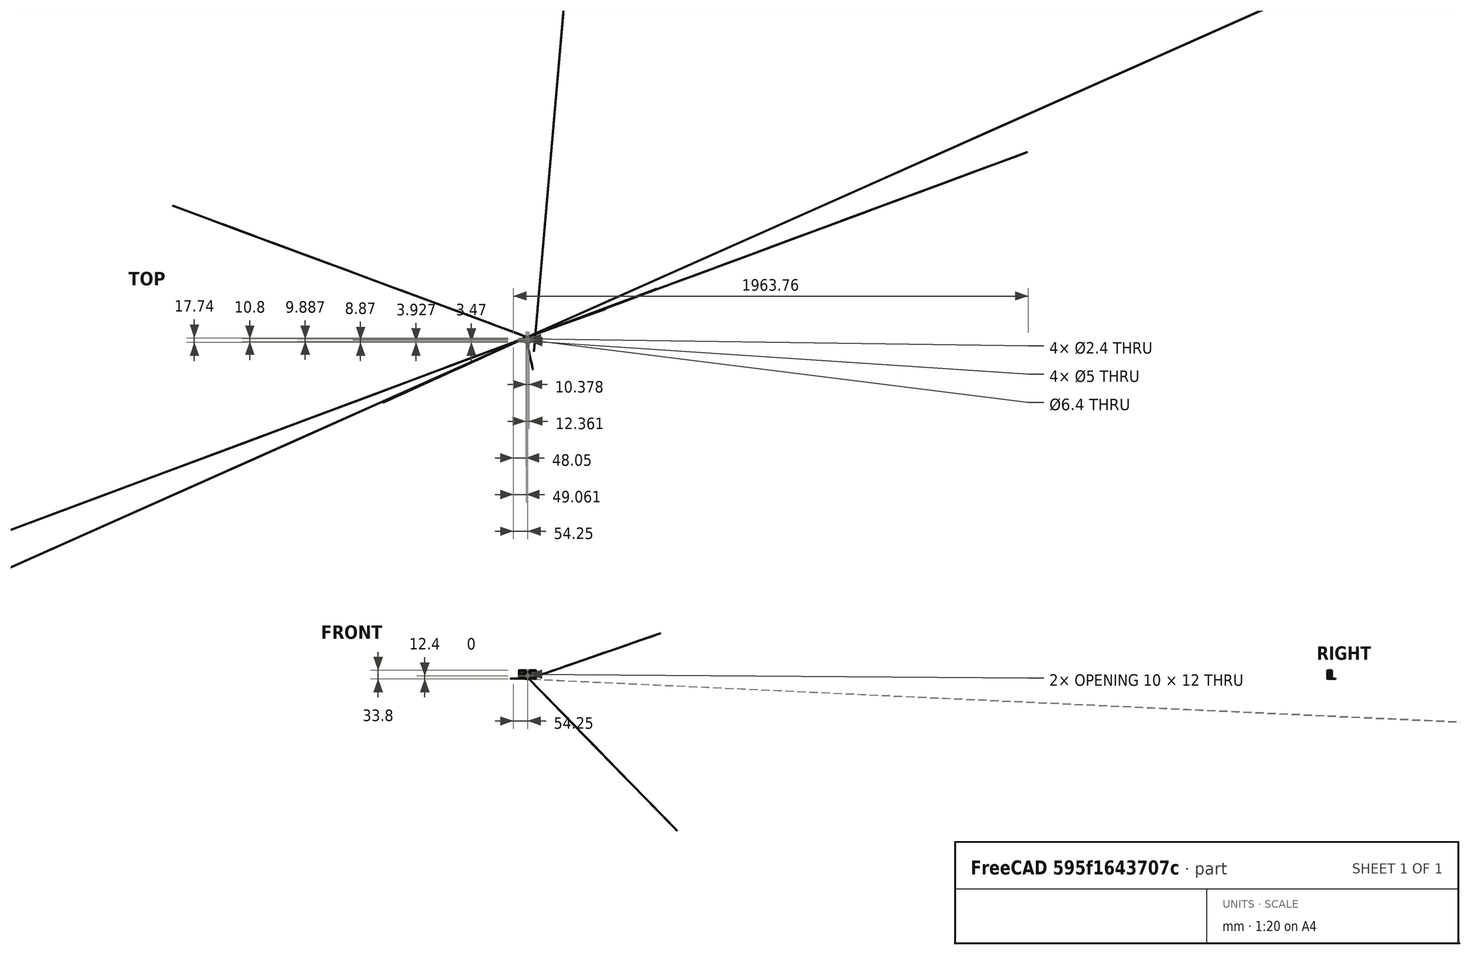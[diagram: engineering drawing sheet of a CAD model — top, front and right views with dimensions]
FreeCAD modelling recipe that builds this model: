
FCSTD DOCUMENT  (FreeCAD 0.19R0.19.2)
Label: 058
License: All rights reserved
LicenseURL: http://en.wikipedia.org/wiki/All_rights_reserved
objects: Sketcher::SketchObject×6, Part::Extrusion×6, Part::Cut×4, Part::Chamfer×3, Part::MultiFuse×1, Part::Fillet×1
note: 21 computed .brp shape members not serialized (recipe doc carries the construction recipe); baked Part::Feature solids carry a one-line shape summary decoded from their .brp

FEATURE [Sketcher::SketchObject] Sketch  label="main001"
  FullyConstrained = true
  sketch-geometry (68):
    g0: ArcOfCircle CenterX=-3.45031e-07 CenterY=-7.80683e-07 CenterZ=0 NormalX=0 NormalY=0 NormalZ=1 AngleXU=0 Radius=11.6 StartAngle=2.27101 EndAngle=2.66709
    g1: ArcOfCircle CenterX=-3.45031e-07 CenterY=-7.80687e-07 CenterZ=0 NormalX=0 NormalY=0 NormalZ=1 AngleXU=0 Radius=11.6 StartAngle=5.4126 EndAngle=5.80868
    g2: LineSegment StartX=-7.4748 StartY=8.87059 StartZ=0 EndX=7.4748 EndY=8.87059 EndZ=0
    g3: LineSegment StartX=-7.4748 StartY=-8.87059 StartZ=0 EndX=7.4748 EndY=-8.87059 EndZ=0
    g4: ArcOfCircle CenterX=-3.45031e-07 CenterY=-7.80683e-07 CenterZ=0 NormalX=0 NormalY=0 NormalZ=1 AngleXU=0 Radius=11.6 StartAngle=3.6161 EndAngle=4.01218
    g5: ArcOfCircle CenterX=-3.45031e-07 CenterY=-7.80687e-07 CenterZ=0 NormalX=0 NormalY=0 NormalZ=1 AngleXU=0 Radius=11.6 StartAngle=0.474503 EndAngle=0.870585
    g6: ArcOfCircle CenterX=-3.45031e-07 CenterY=-7.80683e-07 CenterZ=0 NormalX=0 NormalY=0 NormalZ=1 AngleXU=0 Radius=10.34 StartAngle=2.27101 EndAngle=4.01218
    g7: ArcOfCircle CenterX=-3.45031e-07 CenterY=-7.80683e-07 CenterZ=0 NormalX=0 NormalY=0 NormalZ=1 AngleXU=0 Radius=10.34 StartAngle=5.4126 EndAngle=7.15377
    g8: LineSegment StartX=-6.66287 StartY=7.90707 StartZ=0 EndX=6.66287 EndY=7.90707 EndZ=0
    g9: LineSegment StartX=-6.66287 StartY=-7.90707 StartZ=0 EndX=6.66287 EndY=-7.90707 EndZ=0
    g10: LineSegment StartX=-28.8 StartY=4.1 StartZ=0 EndX=-30.8 EndY=4.1 EndZ=0
    g11: BSplineCurve PolesCount=3 KnotsCount=2 Degree=2 IsPeriodic=0
    g12: LineSegment StartX=-30.2 StartY=3.1 StartZ=0 EndX=-32.2 EndY=3.1 EndZ=0
    g13: LineSegment StartX=-30.2 StartY=3.1 StartZ=0 EndX=-12.7274 EndY=3.1 EndZ=0
    g14: LineSegment StartX=-28.8 StartY=-4.1 StartZ=0 EndX=-30.8 EndY=-4.1 EndZ=0
    g15: BSplineCurve PolesCount=3 KnotsCount=2 Degree=2 IsPeriodic=0
    g16: LineSegment StartX=-30.2 StartY=-3.1 StartZ=0 EndX=-32.2 EndY=-3.1 EndZ=0
    g17: LineSegment StartX=-30.2 StartY=-3.1 StartZ=0 EndX=-12.7274 EndY=-3.1 EndZ=0
    g18: LineSegment StartX=28.8 StartY=4.1 StartZ=0 EndX=30.8 EndY=4.1 EndZ=0
    g19: BSplineCurve PolesCount=3 KnotsCount=2 Degree=2 IsPeriodic=0
    g20: LineSegment StartX=30.2 StartY=3.1 StartZ=0 EndX=32.2 EndY=3.1 EndZ=0
    g21: LineSegment StartX=30.2 StartY=3.1 StartZ=0 EndX=12.7274 EndY=3.1 EndZ=0
    g22: LineSegment StartX=28.8 StartY=-4.1 StartZ=0 EndX=30.8 EndY=-4.1 EndZ=0
    g23: BSplineCurve PolesCount=3 KnotsCount=2 Degree=2 IsPeriodic=0
    g24: LineSegment StartX=30.2 StartY=-3.1 StartZ=0 EndX=32.2 EndY=-3.1 EndZ=0
    g25: LineSegment StartX=30.2 StartY=-3.1 StartZ=0 EndX=12.7274 EndY=-3.1 EndZ=0
    g26-g30: Circle x5 (B-spline internal-alignment scaffolding for g31; pole/knot coordinates omitted)
    g31: BSplineCurve PolesCount=5 KnotsCount=3 Degree=3 IsPeriodic=0
    g32: GeomPoint X=-12.7274 Y=3.1 Z=0
    g33: GeomPoint X=-11.4637 Y=2.50004e-07 Z=0
    g34: GeomPoint X=-12.7274 Y=-3.1 Z=0
    g35-g39: Circle x5 (B-spline internal-alignment scaffolding for g40; pole/knot coordinates omitted)
    g40: BSplineCurve PolesCount=5 KnotsCount=3 Degree=3 IsPeriodic=0
    g41: GeomPoint X=12.7274 Y=-3.1 Z=0
    g42: GeomPoint X=11.4637 Y=2.49999e-07 Z=0
    g43: GeomPoint X=12.7274 Y=3.1 Z=0
    g44: Circle CenterX=-28.8 CenterY=4.1 CenterZ=0 NormalX=0 NormalY=0 NormalZ=1 AngleXU=0 Radius=1
    g45: Circle CenterX=-10.3184 CenterY=4.4 CenterZ=0 NormalX=0 NormalY=0 NormalZ=1 AngleXU=0 Radius=1
    g46: Circle CenterX=-10.3184 CenterY=5.3 CenterZ=0 NormalX=0 NormalY=0 NormalZ=1 AngleXU=0 Radius=1
    g47: BSplineCurve PolesCount=3 KnotsCount=2 Degree=2 IsPeriodic=0
    g48: GeomPoint X=-28.8 Y=4.1 Z=0
    g49: GeomPoint X=-10.3184 Y=5.3 Z=0
    g50: Circle CenterX=-28.8 CenterY=-4.1 CenterZ=0 NormalX=0 NormalY=0 NormalZ=1 AngleXU=0 Radius=1
    g51: Circle CenterX=-10.3184 CenterY=-4.4 CenterZ=0 NormalX=0 NormalY=0 NormalZ=1 AngleXU=0 Radius=1
    g52: Circle CenterX=-10.3184 CenterY=-5.3 CenterZ=0 NormalX=0 NormalY=0 NormalZ=1 AngleXU=0 Radius=1
    g53: BSplineCurve PolesCount=3 KnotsCount=2 Degree=2 IsPeriodic=0
    g54: GeomPoint X=-28.8 Y=-4.1 Z=0
    g55: GeomPoint X=-10.3184 Y=-5.3 Z=0
    g56: Circle CenterX=28.8 CenterY=4.1 CenterZ=0 NormalX=0 NormalY=0 NormalZ=1 AngleXU=0 Radius=1
    g57: Circle CenterX=10.3184 CenterY=4.4 CenterZ=0 NormalX=0 NormalY=0 NormalZ=1 AngleXU=0 Radius=1
    g58: Circle CenterX=10.3184 CenterY=5.3 CenterZ=0 NormalX=0 NormalY=0 NormalZ=1 AngleXU=0 Radius=1
    g59: BSplineCurve PolesCount=3 KnotsCount=2 Degree=2 IsPeriodic=0
    g60: GeomPoint X=28.8 Y=4.1 Z=0
    g61: GeomPoint X=10.3184 Y=5.3 Z=0
    g62: Circle CenterX=28.8 CenterY=-4.1 CenterZ=0 NormalX=0 NormalY=0 NormalZ=1 AngleXU=0 Radius=1
    g63: Circle CenterX=10.3184 CenterY=-4.4 CenterZ=0 NormalX=0 NormalY=0 NormalZ=1 AngleXU=0 Radius=1
    g64: Circle CenterX=10.3184 CenterY=-5.3 CenterZ=0 NormalX=0 NormalY=0 NormalZ=1 AngleXU=0 Radius=1
    g65: BSplineCurve PolesCount=3 KnotsCount=2 Degree=2 IsPeriodic=0
    g66: GeomPoint X=28.8 Y=-4.1 Z=0
    g67: GeomPoint X=10.3184 Y=-5.3 Z=0
  constraints (114):
    c: Block(g1)
    c: Block(g0)
    c: Coincident(g2,g0)
    c: Coincident(g2,g5)
    c: Horizontal(g2)
    c: Coincident(g3,g4)
    c: Coincident(g3,g1)
    c: Horizontal(g3)
    c: Equal(g0,g4)
    c: Coincident(g0,g4)
    c: Equal(g1,g5)
    c: Coincident(g1,g5)
    c: Block(g4)
    c: Block(g5)
    c: Coincident(g6,g0)
    c: Coincident(g7,g0)
    c: Block(g7)
    c: Block(g6)
    c: Coincident(g8,g6)
    c: Coincident(g8,g7)
    c: Horizontal(g8)
    c: Coincident(g9,g6)
    c: Coincident(g9,g7)
    c: Horizontal(g9)
    c: Block(g13)
    c: Coincident(g12,g13)
    c: Horizontal(g12)
    c: Block(g11)
    c: Coincident(g11,g12)
    c: Coincident(g10,g11)
    c: Horizontal(g10)
    c: Block(g17)
    c: Horizontal(g16)
    c: Coincident(g16,g17)
    c: Block(g15)
    c: Coincident(g15,g16)
    c: Coincident(g14,g15)
    c: Horizontal(g14)
    c: Block(g21)
    c: Coincident(g20,g21)
    c: Horizontal(g20)
    c: Block(g19)
    c: Coincident(g19,g20)
    c: Coincident(g18,g19)
    c: Horizontal(g18)
    c: Block(g25)
    c: Horizontal(g24)
    c: Coincident(g24,g25)
    c: Block(g23)
    c: Coincident(g23,g24)
    c: Coincident(g22,g23)
    c: Horizontal(g22)
    c: Coincident(g31,g13)
    c: Weight(g26) = 1
    c: Equal(g26, g27-g30) x4
    c: Coincident(g31,g17)
    c: InternalAlignment(g26-g30 -> g31) x5
    c: InternalAlignment(g32,g31)
    c: InternalAlignment(g33,g31)
    c: InternalAlignment(g34,g31)
    c: Block(g31)
    c: Coincident(g40,g25)
    c: Weight(g35) = 1
    c: Equal(g35, g36-g39) x4
    c: Coincident(g40,g21)
    c: InternalAlignment(g35-g39 -> g40) x5
    c: InternalAlignment(g41,g40)
    c: InternalAlignment(g42,g40)
    c: InternalAlignment(g43,g40)
    c: Block(g40)
    c: Coincident(g47,g10)
    c: Weight(g44) = 1
    c: Equal(g44,g45)
    c: Equal(g44,g46)
    c: Coincident(g47,g0)
    c: InternalAlignment(g44,g47)
    c: InternalAlignment(g45,g47)
    c: InternalAlignment(g46,g47)
    c: InternalAlignment(g48,g47)
    c: InternalAlignment(g49,g47)
    c: Block(g47)
    c: Coincident(g53,g14)
    c: Weight(g50) = 1
    c: Equal(g50,g51)
    c: Equal(g50,g52)
    c: Coincident(g53,g4)
    c: InternalAlignment(g50,g53)
    c: InternalAlignment(g51,g53)
    c: InternalAlignment(g52,g53)
    c: InternalAlignment(g54,g53)
    c: InternalAlignment(g55,g53)
    c: Coincident(g59,g18)
    c: Weight(g56) = 1
    c: Equal(g56,g57)
    c: Equal(g56,g58)
    c: Coincident(g59,g5)
    c: InternalAlignment(g56,g59)
    c: InternalAlignment(g57,g59)
    c: InternalAlignment(g58,g59)
    c: InternalAlignment(g60,g59)
    c: InternalAlignment(g61,g59)
    c: Coincident(g65,g22)
    c: Weight(g62) = 1
    c: Equal(g62,g63)
    c: Equal(g62,g64)
    c: Coincident(g65,g1)
    c: InternalAlignment(g62,g65)
    c: InternalAlignment(g63,g65)
    c: InternalAlignment(g64,g65)
    c: InternalAlignment(g66,g65)
    c: InternalAlignment(g67,g65)
    c: Block(g53)
    c: Block(g65)
    c: Block(g59)
FEATURE [Part::Extrusion] Extrude  label="main"
  Base = -> Sketch
  Dir = (0,0,1)
  DirMode = 2
  FaceMakerClass = Part::FaceMakerBullseye
  LengthFwd = 32
  LengthRev = 0
  Solid = true
  Symmetric = false
FEATURE [Sketcher::SketchObject] Sketch001  label="mainCollingAndStructuralHoles"
  FullyConstrained = true
  Placement = pos=(0,0,0) rot=(-1,0,0;4.71239rad)
  sketch-geometry (24):
    g0: Circle CenterX=-5 CenterY=2 CenterZ=0 NormalX=0 NormalY=0 NormalZ=1 AngleXU=0 Radius=1
    g1: Circle CenterX=-5 CenterY=0 CenterZ=0 NormalX=0 NormalY=0 NormalZ=1 AngleXU=0 Radius=1
    g2: Circle CenterX=-3 CenterY=4.6505e-12 CenterZ=0 NormalX=0 NormalY=0 NormalZ=1 AngleXU=0 Radius=1
    g3: BSplineCurve PolesCount=3 KnotsCount=2 Degree=2 IsPeriodic=0
    g4: GeomPoint X=-5 Y=2 Z=0
    g5: GeomPoint X=-3 Y=4.6505e-12 Z=0
    g6: Circle CenterX=5 CenterY=2 CenterZ=0 NormalX=0 NormalY=0 NormalZ=1 AngleXU=0 Radius=1
    g7: Circle CenterX=5 CenterY=4.6505e-12 CenterZ=0 NormalX=0 NormalY=0 NormalZ=1 AngleXU=0 Radius=1
    g8: Circle CenterX=3 CenterY=4.6505e-12 CenterZ=0 NormalX=0 NormalY=0 NormalZ=1 AngleXU=0 Radius=1
    g9: BSplineCurve PolesCount=3 KnotsCount=2 Degree=2 IsPeriodic=0
    g10: GeomPoint X=5 Y=2 Z=0
    g11: GeomPoint X=3 Y=4.6505e-12 Z=0
    g12: LineSegment StartX=5 StartY=2 StartZ=0 EndX=5 EndY=10 EndZ=0
    g13: LineSegment StartX=-5 StartY=2 StartZ=0 EndX=-5 EndY=10 EndZ=0
    g14: LineSegment StartX=-3 StartY=4.6505e-12 StartZ=0 EndX=3 EndY=4.6505e-12 EndZ=0
    g15: LineSegment StartX=-5 StartY=10 StartZ=0 EndX=5 EndY=10 EndZ=0
    g16: BSplineCurve PolesCount=3 KnotsCount=2 Degree=2 IsPeriodic=0
    g17: LineSegment StartX=-3.6 StartY=-18.4 StartZ=0 EndX=3.6 EndY=-18.4 EndZ=0
    g18: BSplineCurve PolesCount=3 KnotsCount=2 Degree=2 IsPeriodic=0
    g19: BSplineCurve PolesCount=3 KnotsCount=2 Degree=2 IsPeriodic=0
    g20: LineSegment StartX=-3.6 StartY=-6.4 StartZ=0 EndX=3.6 EndY=-6.4 EndZ=0
    g21: BSplineCurve PolesCount=3 KnotsCount=2 Degree=2 IsPeriodic=0
    g22: LineSegment StartX=5 StartY=-17 StartZ=0 EndX=5 EndY=-7.8 EndZ=0
    g23: LineSegment StartX=-5 StartY=-7.8 StartZ=0 EndX=-5 EndY=-17 EndZ=0
  constraints (47):
    c: Weight(g0) = 1
    c: Equal(g0,g1)
    c: Equal(g0,g2)
    c: InternalAlignment(g0,g3)
    c: InternalAlignment(g1,g3)
    c: InternalAlignment(g2,g3)
    c: InternalAlignment(g4,g3)
    c: InternalAlignment(g5,g3)
    c: Weight(g6) = 1
    c: Equal(g6,g7)
    c: Equal(g6,g8)
    c: InternalAlignment(g6,g9)
    c: InternalAlignment(g7,g9)
    c: InternalAlignment(g8,g9)
    c: InternalAlignment(g10,g9)
    c: InternalAlignment(g11,g9)
    c: Block(g3)
    c: Coincident(g13,g3)
    c: Block(g9)
    c: Coincident(g12,g9)
    c: Vertical(g12)
    c: Block(g12)
    c: Block(g13)
    c: Coincident(g14,g3)
    c: Coincident(g14,g9)
    c: Horizontal(g14)
    c: Coincident(g15,g13)
    c: Coincident(g15,g12)
    c: Horizontal(g15)
    c: Distance(g12) = 8
    c: Distance(g15) = 10
    c: Block(g16)
    c: Block(g18)
    c: Coincident(g17,g18)
    c: Coincident(g17,g16)
    c: Horizontal(g17)
    c: Block(g19)
    c: Block(g21)
    c: Coincident(g20,g21)
    c: Coincident(g20,g19)
    c: Horizontal(g20)
    c: Coincident(g22,g16)
    c: Coincident(g22,g19)
    c: Vertical(g22)
    c: Coincident(g23,g21)
    c: Coincident(g23,g18)
    c: Vertical(g23)
FEATURE [Part::Extrusion] Extrude001  label="mainCollingAndStructuralHoles001"
  Base = -> Sketch001
  Dir = (0,-1,3e-16)
  DirMode = 2
  FaceMakerClass = Part::FaceMakerBullseye
  LengthFwd = 20
  LengthRev = 0
  Placement = pos=(0,10,23) rot=(0,0,1;0rad)
  Solid = true
  Symmetric = false
FEATURE [Sketcher::SketchObject] Sketch002  label="structuralHoles"
  FullyConstrained = true
  Placement = pos=(0,0,0) rot=(-1,0,0;4.71239rad)
  sketch-geometry (35):
    g0: LineSegment StartX=-28.43 StartY=13.1 StartZ=0 EndX=-28.43 EndY=4.4 EndZ=0
    g1: LineSegment StartX=-28.43 StartY=27.6 StartZ=0 EndX=-28.43 EndY=18.9 EndZ=0
    g2: Circle CenterX=-28.43 CenterY=27.6 CenterZ=0 NormalX=0 NormalY=0 NormalZ=1 AngleXU=0 Radius=1
    g3: Circle CenterX=-28.43 CenterY=29 CenterZ=0 NormalX=0 NormalY=0 NormalZ=1 AngleXU=0 Radius=1
    g4: Circle CenterX=-27.03 CenterY=29 CenterZ=0 NormalX=0 NormalY=0 NormalZ=1 AngleXU=0 Radius=1
    g5: BSplineCurve PolesCount=3 KnotsCount=2 Degree=2 IsPeriodic=0
    g6: GeomPoint X=-28.43 Y=27.6 Z=0
    g7: GeomPoint X=-27.03 Y=29 Z=0
    g8: Circle CenterX=-27.03 CenterY=17.5 CenterZ=0 NormalX=0 NormalY=0 NormalZ=1 AngleXU=0 Radius=1
    g9: Circle CenterX=-28.43 CenterY=17.5 CenterZ=0 NormalX=0 NormalY=0 NormalZ=1 AngleXU=0 Radius=1
    g10: Circle CenterX=-28.43 CenterY=18.9 CenterZ=0 NormalX=0 NormalY=0 NormalZ=1 AngleXU=0 Radius=1
    g11: BSplineCurve PolesCount=3 KnotsCount=2 Degree=2 IsPeriodic=0
    g12: GeomPoint X=-27.03 Y=17.5 Z=0
    g13: GeomPoint X=-28.43 Y=18.9 Z=0
    g14: Circle CenterX=-27.03 CenterY=14.5 CenterZ=0 NormalX=0 NormalY=0 NormalZ=1 AngleXU=0 Radius=1
    g15: Circle CenterX=-28.43 CenterY=14.5 CenterZ=0 NormalX=0 NormalY=0 NormalZ=1 AngleXU=0 Radius=1
    g16: Circle CenterX=-28.43 CenterY=13.1 CenterZ=0 NormalX=0 NormalY=0 NormalZ=1 AngleXU=0 Radius=1
    g17: BSplineCurve PolesCount=3 KnotsCount=2 Degree=2 IsPeriodic=0
    g18: GeomPoint X=-27.03 Y=14.5 Z=0
    g19: GeomPoint X=-28.43 Y=13.1 Z=0
    g20: Circle CenterX=-27.03 CenterY=3 CenterZ=0 NormalX=0 NormalY=0 NormalZ=1 AngleXU=0 Radius=1
    g21: Circle CenterX=-28.43 CenterY=3 CenterZ=0 NormalX=0 NormalY=0 NormalZ=1 AngleXU=0 Radius=1
    g22: Circle CenterX=-28.43 CenterY=4.4 CenterZ=0 NormalX=0 NormalY=0 NormalZ=1 AngleXU=0 Radius=1
    g23: BSplineCurve PolesCount=3 KnotsCount=2 Degree=2 IsPeriodic=0
    g24: GeomPoint X=-28.43 Y=4.4 Z=0
    g25: BSplineCurve PolesCount=3 KnotsCount=2 Degree=2 IsPeriodic=0
    g26: BSplineCurve PolesCount=3 KnotsCount=2 Degree=2 IsPeriodic=0
    g27: LineSegment StartX=-11.73 StartY=12.1 StartZ=0 EndX=-11.73 EndY=6.4 EndZ=0
    g28: BSplineCurve PolesCount=3 KnotsCount=2 Degree=2 IsPeriodic=0
    g29: BSplineCurve PolesCount=3 KnotsCount=2 Degree=2 IsPeriodic=0
    g30: LineSegment StartX=-11.73 StartY=25.6 StartZ=0 EndX=-11.73 EndY=19.9 EndZ=0
    g31: LineSegment StartX=-27.03 StartY=14.5 StartZ=0 EndX=-13.13 EndY=13.5 EndZ=0
    g32: LineSegment StartX=-27.03 StartY=3 StartZ=0 EndX=-13.13 EndY=5 EndZ=0
    g33: LineSegment StartX=-27.03 StartY=17.5 StartZ=0 EndX=-13.13 EndY=18.5 EndZ=0
    g34: LineSegment StartX=-27.03 StartY=29 StartZ=0 EndX=-13.13 EndY=27 EndZ=0
  constraints (61):
    c: Distance(g0) = 8.7
    c: Vertical(g0)
    c: Equal(g0,g1) = 8.7
    c: Vertical(g1)
    c: Weight(g2) = 1
    c: Equal(g2,g3)
    c: Equal(g2,g4)
    c: InternalAlignment(g2,g5)
    c: InternalAlignment(g3,g5)
    c: InternalAlignment(g4,g5)
    c: InternalAlignment(g6,g5)
    c: InternalAlignment(g7,g5)
    c: Weight(g8) = 1
    c: Equal(g8,g9)
    c: Equal(g8,g10)
    c: Coincident(g11,g1)
    c: InternalAlignment(g8,g11)
    c: InternalAlignment(g9,g11)
    c: InternalAlignment(g10,g11)
    c: InternalAlignment(g12,g11)
    c: InternalAlignment(g13,g11)
    c: Weight(g14) = 1
    c: Equal(g14,g15)
    c: Equal(g14,g16)
    c: Coincident(g17,g0)
    c: InternalAlignment(g14,g17)
    c: InternalAlignment(g15,g17)
    c: InternalAlignment(g16,g17)
    c: InternalAlignment(g18,g17)
    c: InternalAlignment(g19,g17)
    c: Weight(g20) = 1
    c: Equal(g20,g21)
    c: Equal(g20,g22)
    c: InternalAlignment(g20,g23)
    c: InternalAlignment(g21,g23)
    c: InternalAlignment(g22,g23)
    c: InternalAlignment(g24,g23)
    c: Block(g23)
    c: Block(g5)
    c: Block(g1)
    c: Block(g11)
    c: Block(g0)
    c: Block(g17)
    c: Vertical(g27)
    c: Coincident(g25,g27)
    c: Block(g27)
    c: Block(g25)
    c: Block(g26)
    c: Vertical(g30)
    c: Coincident(g28,g30)
    c: Block(g30)
    c: Block(g28)
    c: Block(g29)
    c: Coincident(g31,g17)
    c: Coincident(g31,g25)
    c: Coincident(g32,g23)
    c: Coincident(g32,g26)
    c: Coincident(g33,g11)
    c: Coincident(g33,g28)
    c: Coincident(g34,g5)
    c: Coincident(g34,g29)
FEATURE [Part::Extrusion] Extrude002  label="structuralHolesLeft"
  Base = -> Sketch002
  Dir = (0,-1,3e-16)
  DirMode = 2
  FaceMakerClass = Part::FaceMakerBullseye
  LengthFwd = 20
  LengthRev = 0
  Placement = pos=(0,10,0) rot=(0,0,1;0rad)
  Solid = true
  Symmetric = false
FEATURE [Sketcher::SketchObject] Sketch005  label="mainFront"
  FullyConstrained = true
  sketch-geometry (13):
    g0: LineSegment StartX=-7.4748 StartY=8.87059 StartZ=0 EndX=7.4748 EndY=8.87059 EndZ=0
    g1: LineSegment StartX=-7.4748 StartY=-8.87059 StartZ=0 EndX=7.4748 EndY=-8.87059 EndZ=0
    g2: ArcOfCircle CenterX=-3.45031e-07 CenterY=0 CenterZ=0 NormalX=0 NormalY=0 NormalZ=1 AngleXU=0 Radius=11.6 StartAngle=2.27101 EndAngle=4.01218
    g3: ArcOfCircle CenterX=-3.45031e-07 CenterY=0 CenterZ=0 NormalX=0 NormalY=0 NormalZ=1 AngleXU=0 Radius=11.6 StartAngle=5.4126 EndAngle=7.15377
    g4: Circle CenterX=-3.45031e-07 CenterY=0 CenterZ=0 NormalX=0 NormalY=0 NormalZ=1 AngleXU=0 Radius=3.2
    g5: Circle CenterX=-5.18896 CenterY=4.94337 CenterZ=0 NormalX=0 NormalY=0 NormalZ=1 AngleXU=0 Radius=2.5
    g6: Circle CenterX=5.18896 CenterY=4.94337 CenterZ=0 NormalX=0 NormalY=0 NormalZ=1 AngleXU=0 Radius=2.5
    g7: Circle CenterX=-3.45031e-07 CenterY=5.4 CenterZ=0 NormalX=0 NormalY=0 NormalZ=1 AngleXU=0 Radius=1.2
    g8: Circle CenterX=-3.45031e-07 CenterY=-5.4 CenterZ=0 NormalX=0 NormalY=0 NormalZ=1 AngleXU=0 Radius=1.2
    g9: Circle CenterX=-5.18896 CenterY=-4.94337 CenterZ=0 NormalX=0 NormalY=0 NormalZ=1 AngleXU=0 Radius=2.5
    g10: Circle CenterX=5.18896 CenterY=-4.94337 CenterZ=0 NormalX=0 NormalY=0 NormalZ=1 AngleXU=0 Radius=2.5
    g11: Circle CenterX=-6.2 CenterY=0 CenterZ=0 NormalX=0 NormalY=0 NormalZ=1 AngleXU=0 Radius=1.2
    g12: Circle CenterX=6.16076 CenterY=0 CenterZ=0 NormalX=0 NormalY=0 NormalZ=1 AngleXU=0 Radius=1.2
  constraints (19):
    c: Block(g0)
    c: Block(g1)
    c: Coincident(g2,g0)
    c: Coincident(g2,g1)
    c: Coincident(g3,g0)
    c: Coincident(g3,g1)
    c: Block(g3)
    c: Block(g2)
    c: Coincident(g4,g2)
    c: Block(g4)
    c: Block(g10)
    c: Block(g8)
    c: Block(g9)
    c: Block(g6)
    c: Block(g7)
    c: Block(g5)
    c: Block(g11)
    c: Block(g12)
    c: PointOnObject(g12,g-1)
FEATURE [Part::Extrusion] Extrude004  label="mainFront001"
  Base = -> Sketch005
  Dir = (0,0,1)
  DirMode = 2
  FaceMakerClass = Part::FaceMakerBullseye
  LengthFwd = 1.8
  LengthRev = 0
  Placement = pos=(0,0,-1.8) rot=(0,0,1;0rad)
  Solid = true
  Symmetric = false
FEATURE [Sketcher::SketchObject] Sketch006  label="structuralHoles003"
  FullyConstrained = true
  Placement = pos=(0,0,0) rot=(1,0,0;1.5708rad)
  sketch-geometry (35):
    g0: LineSegment StartX=-28.43 StartY=13.1 StartZ=0 EndX=-28.43 EndY=4.4 EndZ=0
    g1: LineSegment StartX=-28.43 StartY=27.6 StartZ=0 EndX=-28.43 EndY=18.9 EndZ=0
    g2: Circle CenterX=-28.43 CenterY=27.6 CenterZ=0 NormalX=0 NormalY=0 NormalZ=1 AngleXU=0 Radius=1
    g3: Circle CenterX=-28.43 CenterY=29 CenterZ=0 NormalX=0 NormalY=0 NormalZ=1 AngleXU=0 Radius=1
    g4: Circle CenterX=-27.03 CenterY=29 CenterZ=0 NormalX=0 NormalY=0 NormalZ=1 AngleXU=0 Radius=1
    g5: BSplineCurve PolesCount=3 KnotsCount=2 Degree=2 IsPeriodic=0
    g6: GeomPoint X=-28.43 Y=27.6 Z=0
    g7: GeomPoint X=-27.03 Y=29 Z=0
    g8: Circle CenterX=-27.03 CenterY=17.5 CenterZ=0 NormalX=0 NormalY=0 NormalZ=1 AngleXU=0 Radius=1
    g9: Circle CenterX=-28.43 CenterY=17.5 CenterZ=0 NormalX=0 NormalY=0 NormalZ=1 AngleXU=0 Radius=1
    g10: Circle CenterX=-28.43 CenterY=18.9 CenterZ=0 NormalX=0 NormalY=0 NormalZ=1 AngleXU=0 Radius=1
    g11: BSplineCurve PolesCount=3 KnotsCount=2 Degree=2 IsPeriodic=0
    g12: GeomPoint X=-27.03 Y=17.5 Z=0
    g13: GeomPoint X=-28.43 Y=18.9 Z=0
    g14: Circle CenterX=-27.03 CenterY=14.5 CenterZ=0 NormalX=0 NormalY=0 NormalZ=1 AngleXU=0 Radius=1
    g15: Circle CenterX=-28.43 CenterY=14.5 CenterZ=0 NormalX=0 NormalY=0 NormalZ=1 AngleXU=0 Radius=1
    g16: Circle CenterX=-28.43 CenterY=13.1 CenterZ=0 NormalX=0 NormalY=0 NormalZ=1 AngleXU=0 Radius=1
    g17: BSplineCurve PolesCount=3 KnotsCount=2 Degree=2 IsPeriodic=0
    g18: GeomPoint X=-27.03 Y=14.5 Z=0
    g19: GeomPoint X=-28.43 Y=13.1 Z=0
    g20: Circle CenterX=-27.03 CenterY=3 CenterZ=0 NormalX=0 NormalY=0 NormalZ=1 AngleXU=0 Radius=1
    g21: Circle CenterX=-28.43 CenterY=3 CenterZ=0 NormalX=0 NormalY=0 NormalZ=1 AngleXU=0 Radius=1
    g22: Circle CenterX=-28.43 CenterY=4.4 CenterZ=0 NormalX=0 NormalY=0 NormalZ=1 AngleXU=0 Radius=1
    g23: BSplineCurve PolesCount=3 KnotsCount=2 Degree=2 IsPeriodic=0
    g24: GeomPoint X=-28.43 Y=4.4 Z=0
    g25: BSplineCurve PolesCount=3 KnotsCount=2 Degree=2 IsPeriodic=0
    g26: BSplineCurve PolesCount=3 KnotsCount=2 Degree=2 IsPeriodic=0
    g27: LineSegment StartX=-11.73 StartY=12.1 StartZ=0 EndX=-11.73 EndY=6.4 EndZ=0
    g28: BSplineCurve PolesCount=3 KnotsCount=2 Degree=2 IsPeriodic=0
    g29: BSplineCurve PolesCount=3 KnotsCount=2 Degree=2 IsPeriodic=0
    g30: LineSegment StartX=-11.73 StartY=25.6 StartZ=0 EndX=-11.73 EndY=19.9 EndZ=0
    g31: LineSegment StartX=-27.03 StartY=14.5 StartZ=0 EndX=-13.13 EndY=13.5 EndZ=0
    g32: LineSegment StartX=-27.03 StartY=3 StartZ=0 EndX=-13.13 EndY=5 EndZ=0
    g33: LineSegment StartX=-27.03 StartY=17.5 StartZ=0 EndX=-13.13 EndY=18.5 EndZ=0
    g34: LineSegment StartX=-27.03 StartY=29 StartZ=0 EndX=-13.13 EndY=27 EndZ=0
  constraints (61):
    c: Distance(g0) = 8.7
    c: Vertical(g0)
    c: Equal(g0,g1) = 8.7
    c: Vertical(g1)
    c: Weight(g2) = 1
    c: Equal(g2,g3)
    c: Equal(g2,g4)
    c: InternalAlignment(g2,g5)
    c: InternalAlignment(g3,g5)
    c: InternalAlignment(g4,g5)
    c: InternalAlignment(g6,g5)
    c: InternalAlignment(g7,g5)
    c: Weight(g8) = 1
    c: Equal(g8,g9)
    c: Equal(g8,g10)
    c: Coincident(g11,g1)
    c: InternalAlignment(g8,g11)
    c: InternalAlignment(g9,g11)
    c: InternalAlignment(g10,g11)
    c: InternalAlignment(g12,g11)
    c: InternalAlignment(g13,g11)
    c: Weight(g14) = 1
    c: Equal(g14,g15)
    c: Equal(g14,g16)
    c: Coincident(g17,g0)
    c: InternalAlignment(g14,g17)
    c: InternalAlignment(g15,g17)
    c: InternalAlignment(g16,g17)
    c: InternalAlignment(g18,g17)
    c: InternalAlignment(g19,g17)
    c: Weight(g20) = 1
    c: Equal(g20,g21)
    c: Equal(g20,g22)
    c: InternalAlignment(g20,g23)
    c: InternalAlignment(g21,g23)
    c: InternalAlignment(g22,g23)
    c: InternalAlignment(g24,g23)
    c: Block(g23)
    c: Block(g5)
    c: Block(g1)
    c: Block(g11)
    c: Block(g0)
    c: Block(g17)
    c: Vertical(g27)
    c: Coincident(g25,g27)
    c: Block(g27)
    c: Block(g25)
    c: Block(g26)
    c: Vertical(g30)
    c: Coincident(g28,g30)
    c: Block(g30)
    c: Block(g28)
    c: Block(g29)
    c: Coincident(g31,g17)
    c: Coincident(g31,g25)
    c: Coincident(g32,g23)
    c: Coincident(g32,g26)
    c: Coincident(g33,g11)
    c: Coincident(g33,g28)
    c: Coincident(g34,g5)
    c: Coincident(g34,g29)
FEATURE [Part::Extrusion] Extrude005  label="structuralHolesRight"
  Base = -> Sketch006
  Dir = (0,-1,3e-16)
  DirMode = 2
  FaceMakerClass = Part::FaceMakerBullseye
  LengthFwd = 20
  LengthRev = 0
  Placement = pos=(0,10,32) rot=(0,1,0;3.14159rad)
  Solid = true
  Symmetric = false
FEATURE [Sketcher::SketchObject] Sketch007  label="structuralHolesSide"
  FullyConstrained = true
  Placement = pos=(0,0,0) rot=(0.57735,0.57735,0.57735;2.0944rad)
  sketch-geometry (16):
    g0: BSplineCurve PolesCount=3 KnotsCount=2 Degree=2 IsPeriodic=0
    g1: BSplineCurve PolesCount=3 KnotsCount=2 Degree=2 IsPeriodic=0
    g2: LineSegment StartX=-1.2 StartY=12 StartZ=0 EndX=1.2 EndY=12 EndZ=0
    g3: BSplineCurve PolesCount=3 KnotsCount=2 Degree=2 IsPeriodic=0
    g4: BSplineCurve PolesCount=3 KnotsCount=2 Degree=2 IsPeriodic=0
    g5: LineSegment StartX=-1.2 StartY=8 StartZ=0 EndX=1.2 EndY=8 EndZ=0
    g6: BSplineCurve PolesCount=3 KnotsCount=2 Degree=2 IsPeriodic=0
    g7: BSplineCurve PolesCount=3 KnotsCount=2 Degree=2 IsPeriodic=0
    g8: LineSegment StartX=-1.2 StartY=-1 StartZ=0 EndX=1.2 EndY=-1 EndZ=0
    g9: BSplineCurve PolesCount=3 KnotsCount=2 Degree=2 IsPeriodic=0
    g10: BSplineCurve PolesCount=3 KnotsCount=2 Degree=2 IsPeriodic=0
    g11: LineSegment StartX=-1.2 StartY=21 StartZ=0 EndX=1.2 EndY=21 EndZ=0
    g12: LineSegment StartX=-2.6 StartY=19.6 StartZ=0 EndX=-2.6 EndY=13.4 EndZ=0
    g13: LineSegment StartX=2.6 StartY=19.6 StartZ=0 EndX=2.6 EndY=13.4 EndZ=0
    g14: LineSegment StartX=-2.6 StartY=6.6 StartZ=0 EndX=-2.6 EndY=0.4 EndZ=0
    g15: LineSegment StartX=2.6 StartY=6.6 StartZ=0 EndX=2.6 EndY=0.4 EndZ=0
  constraints (28):
    c: Horizontal(g2)
    c: Block(g1)
    c: Block(g0)
    c: Block(g2)
    c: Horizontal(g5)
    c: Block(g3)
    c: Block(g4)
    c: Block(g5)
    c: Horizontal(g8)
    c: Block(g6)
    c: Block(g7)
    c: Block(g8)
    c: Horizontal(g11)
    c: Block(g10)
    c: Block(g9)
    c: Block(g11)
    c: Coincident(g12,g9)
    c: Coincident(g12,g0)
    c: Vertical(g12)
    c: Coincident(g13,g10)
    c: Coincident(g13,g1)
    c: Vertical(g13)
    c: Coincident(g14,g4)
    c: Coincident(g14,g7)
    c: Vertical(g14)
    c: Coincident(g15,g3)
    c: Coincident(g15,g6)
    c: Vertical(g15)
FEATURE [Part::Extrusion] Extrude006  label="structuralHolesSide001"
  Base = -> Sketch007
  Dir = (1,0,0)
  DirMode = 2
  FaceMakerClass = Part::FaceMakerBullseye
  LengthFwd = 28
  LengthRev = 0
  Placement = pos=(-14,0,6) rot=(0,0,1;0rad)
  Solid = true
  Symmetric = false
FEATURE [Part::Cut] Cut  label="main002"
  Base = -> Extrude
  Tool = -> Extrude001
FEATURE [Part::Cut] Cut001  label="main003"
  Base = -> Cut
  Tool = -> Extrude002
FEATURE [Part::Cut] Cut002  label="main004"
  Base = -> Cut001
  Tool = -> Extrude005
FEATURE [Part::Cut] Cut003  label="main005"
  Base = -> Cut002
  Tool = -> Extrude006
FEATURE [Part::MultiFuse] Fusion  label="main006"
  Shapes = -> [Extrude004,Cut003]
FEATURE [Part::Chamfer] Chamfer
  Base = -> Fusion
  Edges = 4 edges r=1: [Edge3,Edge12,Edge16,Edge19]
FEATURE [Part::Chamfer] Chamfer001
  Base = -> Chamfer
  Edges = 4 edges r=0.42: [Edge72,Edge73,Edge74,Edge75]
FEATURE [Part::Chamfer] Chamfer002
  Base = -> Chamfer001
  Edges = 2 edges r=0.99: [Edge9,Edge10]
FEATURE [Part::Fillet] Fillet
  Base = -> Chamfer002
  Edges = 4 edges r=1: [Edge19,Edge21,Edge24,Edge25]
